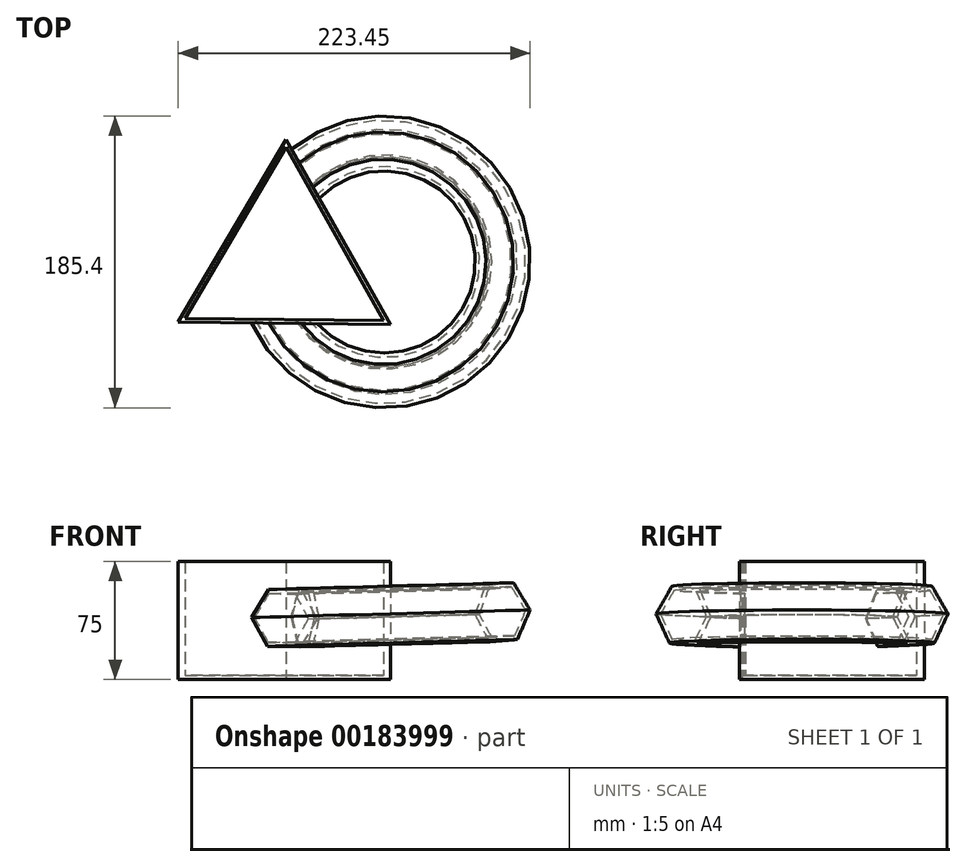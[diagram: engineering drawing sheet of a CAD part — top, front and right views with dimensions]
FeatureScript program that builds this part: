
annotation { "Feature Type Name" : "Feature", "Feature Type Description" : "" }
export const myFeature = defineFeature(function(context is Context, id is Id, definition is map)
    precondition{}
    {
        {
            var Q0;
            Q0=qCreatedBy(makeId("Top.planeOp"),FACE);
            var sketch = newSketch(context, id + "F0", { "sketchPlane" : qUnion([Q0])});
            skCircle(sketch, "E0.cCircle", {"center": v(0, 0) * mm, "radius": 38.92 * mm, "construction": true});
            skLineSegment(sketch, "E0.0", {"start": v(-67.8, -38.24) * mm, "end": v(0.79, 77.84) * mm});
            skLineSegment(sketch, "E0.1", {"start": v(0.79, 77.84) * mm, "end": v(67.01, -39.6) * mm});
            skLineSegment(sketch, "E0.2", {"start": v(67.01, -39.6) * mm, "end": v(-67.8, -38.24) * mm});
            skPoint(sketch, "E0.0.midPoint", {"position": v(-33.5, 19.8) * mm});
            skSolve(sketch);
        }
        {
            var Q0;
            Q0=makeQuery(id+"F0.imprint","IMPRINT",FACE,{"disambiguationData":[TD([[makeQuery(id+"F0.imprint","IMPRINT",EDGE,{"derivedFrom":sQuery(id+"F0.wireOp",EDGE,"E0.0")}),-1.0]])]});
            extrude(context, id + "F1", {"entities" : qUnion([Q0]), "depth" : 75 * mm});
        }
        {
            var Q0;
            Q0=makeQuery(id+"F1.opExtrude","SWEPT_FACE",FACE,{"disambiguationData":[OSD([sQuery(id+"F0.wireOp",EDGE,"E0.2")])]});
            var sketch = newSketch(context, id + "F2", { "sketchPlane" : qUnion([Q0])});
            skCircle(sketch, "E1.cCircle", {"center": v(0, 38.97) * mm, "radius": 18.04 * mm, "construction": true});
            skLineSegment(sketch, "E1.0", {"start": v(20.82, 38.57) * mm, "end": v(10.07, 20.74) * mm});
            skLineSegment(sketch, "E1.1", {"start": v(10.07, 20.74) * mm, "end": v(-10.76, 21.14) * mm});
            skLineSegment(sketch, "E1.2", {"start": v(-10.76, 21.14) * mm, "end": v(-20.82, 39.37) * mm});
            skLineSegment(sketch, "E1.3", {"start": v(-20.82, 39.37) * mm, "end": v(-10.07, 57.2) * mm});
            skLineSegment(sketch, "E1.4", {"start": v(-10.07, 57.2) * mm, "end": v(10.76, 56.8) * mm});
            skLineSegment(sketch, "E1.5", {"start": v(10.76, 56.8) * mm, "end": v(20.82, 38.57) * mm});
            skPoint(sketch, "E1.0.midPoint", {"position": v(15.45, 29.65) * mm});
            skSolve(sketch);
        }
        {
            var Q0;
            Q0=qCreatedBy(makeId("Front.planeOp"),FACE);
            var sketch = newSketch(context, id + "F3", { "sketchPlane" : qUnion([Q0])});
            skLineSegment(sketch, "E2", {"start": v(63.32, 29.14) * mm, "end": v(65.58, -54.3) * mm});
            skSolve(sketch);
        }
        {
            var Q0;
            Q0=makeQuery(id+"F2.imprint","IMPRINT",FACE,{"disambiguationData":[TD([[makeQuery(id+"F2.imprint","IMPRINT",EDGE,{"derivedFrom":sQuery(id+"F2.wireOp",EDGE,"E1.0")}),-1.0]])]});
            var Q1;
            Q1=sQuery(id+"F3.wireOp",EDGE,"E2");
            revolve(context, id + "F4", {"operationType" : NewBodyOperationType.ADD, "entities" : qUnion([Q0]), "axis" : qUnion([Q1]), "revolveType" : RevolveType.FULL});
        }
        {
            var Q0;
            Q0=makeQuery(id+"F1.opExtrude","CAP_FACE",FACE,{"disambiguationData":[OSD([sQuery(id+"F0.wireOp",EDGE,"E0.0"),sQuery(id+"F0.wireOp",EDGE,"E0.1"),sQuery(id+"F0.wireOp",EDGE,"E0.2")])],"isStart":false});
            var sketch = newSketch(context, id + "F5", { "sketchPlane" : qUnion([Q0])});
            skLineSegment(sketch, "E3.bottom", {"start": v(21.01, -39.13) * mm, "end": v(-21.01, -39.13) * mm});
            skLineSegment(sketch, "E3.top", {"start": v(21.01, 39.13) * mm, "end": v(-21.01, 39.13) * mm});
            skLineSegment(sketch, "E3.left", {"start": v(21.01, -39.13) * mm, "end": v(21.01, 39.13) * mm});
            skLineSegment(sketch, "E3.right", {"start": v(-21.01, -39.13) * mm, "end": v(-21.01, 39.13) * mm});
            skPoint(sketch, "E3.middle", {"position": v(0, 0) * mm});
            skSolve(sketch);
        }
        {
            var Q0;
            {var subQ0=sQuery(id+"F5.wireOp",EDGE,"E3.top");Q0=makeQuery(id+"F5.imprint","IMPRINT",FACE,{"disambiguationData":[TD([[makeQuery(id+"F5.imprint","IMPRINT",EDGE,{"derivedFrom":subQ0}),1.0]])]});}
            extrude(context, id + "F6", {"entities" : qUnion([Q0]), "operationType" : NewBodyOperationType.ADD, "oppositeDirection" : true, "depth" : 50 * mm});
        }
        {
            var Q0;
            Q0=makeQuery(id+"F1.opExtrude","CAP_FACE",FACE,{"disambiguationData":[OSD([sQuery(id+"F0.wireOp",EDGE,"E0.0"),sQuery(id+"F0.wireOp",EDGE,"E0.1"),sQuery(id+"F0.wireOp",EDGE,"E0.2")])],"isStart":false});
            shell(context, id + "F7", {"entities" : qUnion([Q0]), "thickness" : 2.5 * mm});
        }
    });
